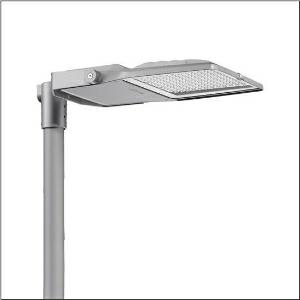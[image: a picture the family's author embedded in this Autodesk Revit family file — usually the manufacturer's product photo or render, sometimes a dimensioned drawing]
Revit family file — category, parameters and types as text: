
# Revit family: floodlight_fl_21_iq_midi___pl61_5xa7781e4c3a_96c8
name_source: partatom
category: Lighting Fixtures
units: mm (PartAtom-declared; Revit-internal decimal feet)

## family parameters
Cut with Voids When Loaded = No
Host = Face
Light Source = No
Part Type = Normal
Room Calculation Point = No
Round Connector Dimension = Use Diameter
Shared = No

## types (1)
- --- (1 x LED, 27490 lm, 208.1 W, 4000K)
    Apparent Load = 208 VA
    CIE Flux Codes = 33 65 98 100 100
    Color Rendering = 70
    Color Temperature = 4000K
    Default Elevation = 1800 mm
    Description = Floodlight FL 21 iQ midi, floodlight, primary light control with lens, of PMMA, primary optical cover: protective disc, of toughened safety glass, transparent, light distribution: PL61, light emission: direct distribution, installation type: surface-mounted, LED, High Power LED, rated luminous flux: 27.490lm, luminous efficacy: 132lm/W, light colour: 740, colour temperature: 4000K, control gear: iQ Comfort/DALI, control: optimised constant luminous flux control (CLO 2.0), Desk-Remote (wireless, voltage-free reading and setting of iQ features in the workshop via application-optimized NFC function/RFID function), Light-Fading, Smart-Wire, Night-Set, Lumen-Switch, Temp-Guard, Auto-Match, with terminal, 6-pole, mains connection: 220..240V, AC, 50/60Hz, start of lifetime: 208W, end of service life: 227W, reduction: 90W, luminaire housing, of diecast aluminium, powder-coated, Siteco® metallic grey (DB 702S), corrosivity category C5 mid according to DIN EN ISO 12944, suitable for swimming pools, chlorine-resistant, sealing non-destructively replaceable, please order mast flange separately, mast bracket, of steel, galvanised, powder-coated, Siteco® metallic grey (DB 702S), protection rating (complete): IP66, insulation class (complete): insulation class II (safety insulation), certification: CE, ENEC, VDE, protection symbol: D, impact resistance: IK08, permissible operating ambient temperature: -40..+40°C, permissible operating ambient temperature for outdoor applications: -40..+50°C, standard: DIN EN 12944, LABS conformity tested according to VDMA 24364:2018-05, packaging unit: 1 piece

Light Distribution: PL61
    Height = 76 mm
    Lamp = 1 x LED
    Lamp Light Flux = 27490 lm
    Lamp Power = 208.1 W
    Lamp count = 1
    Length = 657 mm
    Luminous efficacy = 132 lm/W
    Manufacturer = Siteco
    ModVariant = No
    Model = 5XA7781E4C3A
    Number of Poles = 1
    OnlyDefault = Yes
    Power Factor = 1
    Product Name = Floodlight FL 21 iQ midi | PL61
    Product group = floodlight | pylon annexe
    ProductGroupID = 6200
    Protection Class = Protection class II
    Protection Degree = IP 66
    RLX_Detail_Level = 1
    RLX_Emergency_Light_Flux = 0 lm
    RLX_Emergency_Type = 0
    RLX_Emergency_Type_DB = No
    RlxData = <blob elided: 153593 chars, md5=4ed101f5>
    Socket = socket
    Standby Power = 0 W
    System Light Flux = 27490 lm
    System Power = 208 W
    Type Comments = factory setting: luminous flux: 100 % | dim-lin: 254 | 710 mA
    Type Image = l_1007123.jpg
    URL = http://relux.com
    VarID = @adj_108862
    Voltage = 0 V
    Weight = 0.00 kg
    Width = 442 mm

## geometry (parser evidence)
native form markers: Blend x4, Sweep x15
no freeform markers — native parametric forms only
